# Revit family: FU_Sandler_Wudi 9-3
name_source: partatom
category: Furniture
units: mm (PartAtom-declared; Revit-internal decimal feet)

## family parameters
Always vertical = Yes
Cut with Voids When Loaded = No
Enable Cutting in Views = No
OmniClass Number = 23.40.20.00
OmniClass Title = General Furniture and Specialties
Render Appearance Source = Family Geometry
Room Calculation Point = No
Shared = No
Work Plane-Based = No

## types (4) — shared parameters
Assembly Code = E2020200
Depth = 450 mm  [stored 1.47638 ft]
Description = Coffee table made of solid oak. 60 x 45cm
Height = 335 mm  [stored 1.09908 ft]
Manufacturer = Sandler
Table Leg Finish = Wood - Oak - Sandler - Walnut - Legs
Table Top = Wood - Oak - Sandler - Walnut - TableTops
URL = https://www.sandlerseating.com
zero-valued in all types: Default Elevation

## per-type parameters (varying)
| type | Shelf Visibility | Width |
| Wudi 9.1 | No | 600 mm |
| Wudi 9.2 | Yes | 600 mm |
| Wudi 9.3 | No | 1200 mm |
| Wudi 9.4 | Yes | 1200 mm |

note: column(s) folded — value = type name in every type: Model

note: [stored X ft] marks values corroborated as IEEE doubles in the binary element streams (Revit-internal decimal feet)

## geometry (parser evidence)
native form markers: Sweep x2
no freeform markers — native parametric forms only
